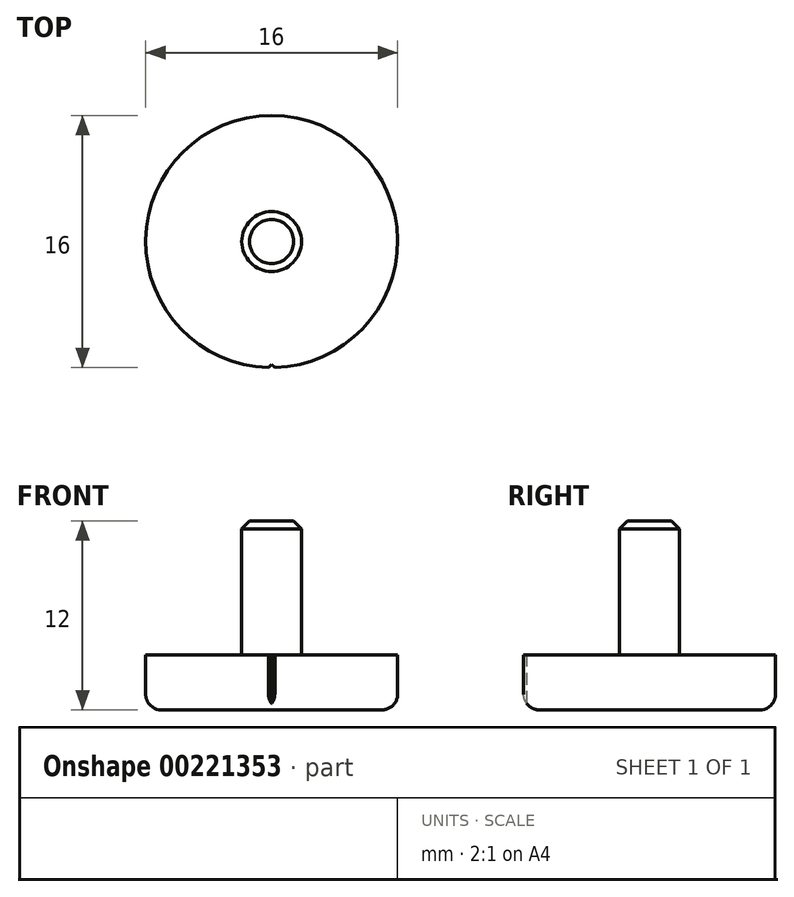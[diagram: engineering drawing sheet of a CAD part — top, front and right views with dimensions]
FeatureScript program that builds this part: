
annotation { "Feature Type Name" : "Feature", "Feature Type Description" : "" }
export const myFeature = defineFeature(function(context is Context, id is Id, definition is map)
    precondition{}
    {
        {
            var Q0;
            Q0=qCreatedBy(makeId("Right.planeOp"),FACE);
            var sketch = newSketch(context, id + "F0", { "sketchPlane" : qUnion([Q0])});
            skLineSegment(sketch, "E0", {"start": v(0, 0) * mm, "end": v(7, 0) * mm});
            skLineSegment(sketch, "E1", {"start": v(8, 1) * mm, "end": v(8, 3.5) * mm});
            skLineSegment(sketch, "E2", {"start": v(8, 3.5) * mm, "end": v(1.9, 3.5) * mm});
            skLineSegment(sketch, "E3", {"start": v(1.9, 3.5) * mm, "end": v(1.9, 12) * mm});
            skLineSegment(sketch, "E4", {"start": v(1.9, 12) * mm, "end": v(0, 12) * mm});
            skLineSegment(sketch, "E5", {"start": v(0, 12) * mm, "end": v(0, 0) * mm});
            skPoint(sketch, "E6.visualSharp", {"position": v(8, 0) * mm});
            skArc(sketch, "E6.filletArc", {"start": v(7, 0) * mm, "mid": v(7.7, 0.3) * mm, "end": v(8, 1) * mm});
            skSolve(sketch);
        }
        {
            var Q0;
            Q0=makeQuery(id+"F0.imprint","IMPRINT",FACE,{"disambiguationData":[TD([[makeQuery(id+"F0.imprint","IMPRINT",EDGE,{"derivedFrom":sQuery(id+"F0.wireOp",EDGE,"E0")}),1.0]])]});
            var Q1;
            Q1=sQuery(id+"F0.wireOp",EDGE,"E5");
            revolve(context, id + "F1", {"surfaceOperationType" : NewSurfaceOperationType.NEW, "entities" : qUnion([Q0]), "axis" : qUnion([Q1]), "revolveType" : RevolveType.FULL});
        }
        {
            var Q0;
            Q0=makeQuery(id+"F1.opRevolve","SWEPT_EDGE",EDGE,{"disambiguationData":[OSD([sQuery(id+"F0.wireOp",EDGE,"E3"),sQuery(id+"F0.wireOp",EDGE,"E4")])]});
            chamfer(context, id + "F2", {"entities" : qUnion([Q0]), "width" : 0.5 * mm, "tangentPropagation" : true});
        }
        {
            var Q0;
            Q0=makeQuery(id+"F1.opRevolve","SWEPT_FACE",FACE,{"disambiguationData":[OSD([sQuery(id+"F0.wireOp",EDGE,"E0")])]});
            var sketch = newSketch(context, id + "F3", { "sketchPlane" : qUnion([Q0])});
            skCircle(sketch, "E7.0", {"center": v(0, 0) * mm, "radius": 8 * mm});
            skLineSegment(sketch, "E8", {"start": v(-0.2, 8) * mm, "end": v(0, 7.8) * mm});
            skLineSegment(sketch, "E9.MirrorCS", {"start": v(0.2, 8) * mm, "end": v(0, 7.8) * mm});
            skSolve(sketch);
        }
        {
            var Q0;
            {var subQ0=sQuery(id+"F3.wireOp",EDGE,"E8");Q0=makeQuery(id+"F3.imprint","IMPRINT",FACE,{"disambiguationData":[TD([[makeQuery(id+"F3.imprint","IMPRINT",EDGE,{"derivedFrom":subQ0}),1.0]])]});}
            extrude(context, id + "F4", {"entities" : qUnion([Q0]), "operationType" : NewBodyOperationType.REMOVE, "oppositeDirection" : true, "depth" : 25 * mm, "offsetDistance" : 25 * mm});
        }
    });
